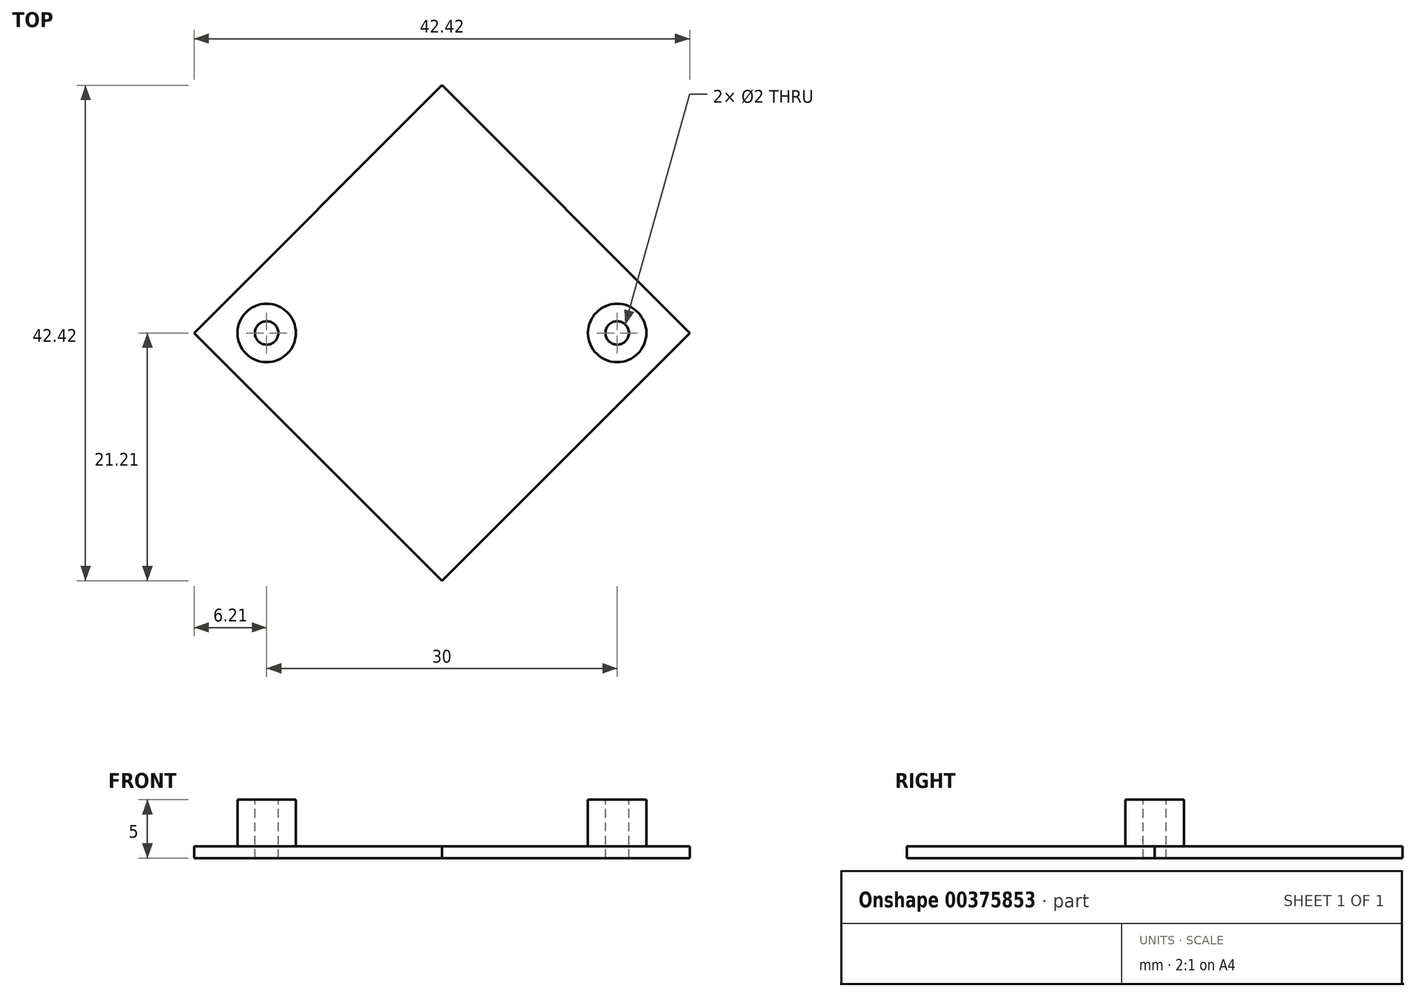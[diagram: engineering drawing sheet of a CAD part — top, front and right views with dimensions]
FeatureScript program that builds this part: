
annotation { "Feature Type Name" : "Feature", "Feature Type Description" : "" }
export const myFeature = defineFeature(function(context is Context, id is Id, definition is map)
    precondition{}
    {
        {
            var Q0;
            Q0=qCreatedBy(makeId("Top.planeOp"),FACE);
            var sketch = newSketch(context, id + "F0", { "sketchPlane" : qUnion([Q0])});
            skLineSegment(sketch, "E0.bottom", {"start": v(0, 21.21) * mm, "end": v(-21.21, 0) * mm});
            skLineSegment(sketch, "E0.top", {"start": v(21.21, 0) * mm, "end": v(0, -21.21) * mm});
            skLineSegment(sketch, "E0.left", {"start": v(0, 21.21) * mm, "end": v(21.21, 0) * mm});
            skLineSegment(sketch, "E0.right", {"start": v(-21.21, 0) * mm, "end": v(0, -21.21) * mm});
            skPoint(sketch, "E0.middle", {"position": v(0, 0) * mm});
            skSolve(sketch);
        }
        {
            var Q0;
            Q0 = qSketchRegion(id + "F0", true);
            extrude(context, id + "F1", {"entities" : qUnion([Q0]), "depth" : 1 * mm});
        }
        {
            var Q0;
            Q0=makeQuery(id+"F1.opExtrude","CAP_FACE",FACE,{"disambiguationData":[OSD([sQuery(id+"F0.wireOp",EDGE,"E0.bottom"),sQuery(id+"F0.wireOp",EDGE,"E0.top"),sQuery(id+"F0.wireOp",EDGE,"E0.left"),sQuery(id+"F0.wireOp",EDGE,"E0.right")])],"isStart":false});
            var sketch = newSketch(context, id + "F2", { "sketchPlane" : qUnion([Q0])});
            skCircle(sketch, "E1", {"center": v(-15, 0) * mm, "radius": 2.5 * mm});
            skCircle(sketch, "E2", {"center": v(15, 0) * mm, "radius": 2.5 * mm});
            skSolve(sketch);
        }
        {
            var Q0;
            Q0 = qSketchRegion(id + "F2", true);
            extrude(context, id + "F3", {"entities" : qUnion([Q0]), "operationType" : NewBodyOperationType.ADD, "depth" : 4 * mm});
        }
        {
            var Q0;
            Q0=makeQuery(id+"F3.opExtrude","CAP_FACE",FACE,{"disambiguationData":[OSD([sQuery(id+"F2.wireOp",EDGE,"E1")])],"isStart":false});
            var sketch = newSketch(context, id + "F4", { "sketchPlane" : qUnion([Q0])});
            skCircle(sketch, "E3", {"center": v(-15, 0) * mm, "radius": 1 * mm});
            skCircle(sketch, "E4", {"center": v(15, 0) * mm, "radius": 1 * mm});
            skSolve(sketch);
        }
        {
            var Q0;
            Q0=makeQuery(id+"F4.imprint","IMPRINT",FACE,{"disambiguationData":[TD([[makeQuery(id+"F4.imprint","IMPRINT",EDGE,{"derivedFrom":sQuery(id+"F4.wireOp",EDGE,"E3")}),1.0]])]});
            var Q1;
            Q1=makeQuery(id+"F4.imprint","IMPRINT",FACE,{"disambiguationData":[TD([[makeQuery(id+"F4.imprint","IMPRINT",EDGE,{"derivedFrom":sQuery(id+"F4.wireOp",EDGE,"E4")}),1.0]])]});
            extrude(context, id + "F5", {"entities" : qUnion([Q0, Q1]), "operationType" : NewBodyOperationType.REMOVE, "oppositeDirection" : true, "depth" : 25 * mm});
        }
    });
